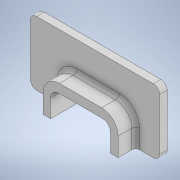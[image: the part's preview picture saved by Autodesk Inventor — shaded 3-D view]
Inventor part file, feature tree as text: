
AUTODESK INVENTOR PART (.ipt)
format: ipt  version: 2021 (Build 250183000, 183)  size: 183,296 bytes
history: native  units: mm
features: extrude x3, fillet x3, sketch x3
ambient origin geometry x8: Origin, YZ Plane, XZ Plane, XY Plane, X Axis, Y Axis, Z Axis, Center Point
bodies: Solid1 (feature_tree)
feature tree (9):
  extrude  "Extrusion1"  Depth=9.5mm
  extrude  "Extrusion2"  Depth=1.285mm
  fillet  "Fillet1"  Radius=1.2mm
  extrude  "Extrusion3"  Depth=1.4mm
  fillet  "Fillet2"  Radius=4.0mm
  fillet  "Fillet3"  Radius=5.0mm
  sketch  "Sketch1"  dims[d0=2.57mm d1=9.5mm]
  sketch  "Sketch2"  dims[d2=1.285mm d3=1.285mm d4=1.2mm]
  sketch  "Sketch3"  dims[d5=1.2mm d6=1.4mm d7=4.0mm d8=0.0mm d9=5.0mm d10=6.0mm d11=6.0mm d12=1.2mm d13=0.0mm d14=2.6mm d15=1.6mm d16=0.0mm d17=0.6mm d18=1.0mm]
